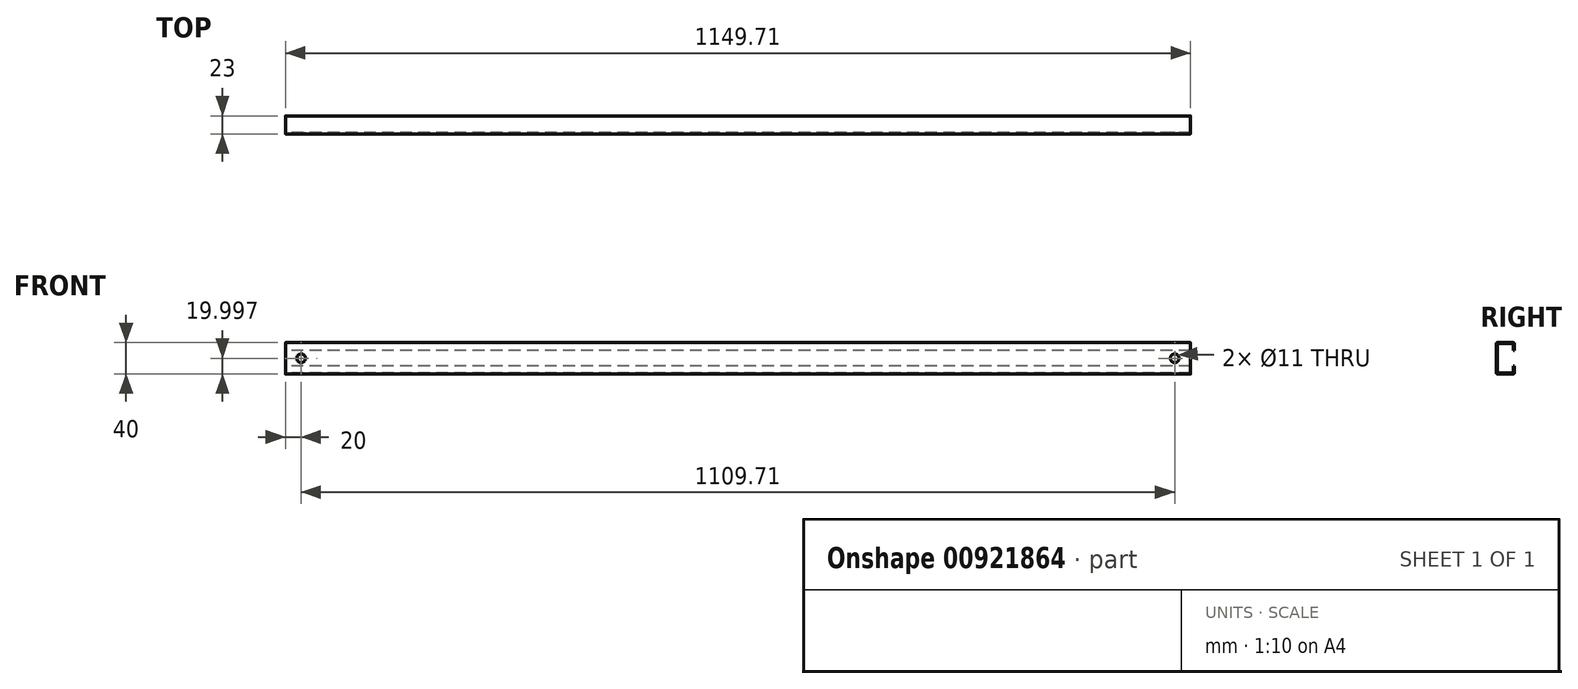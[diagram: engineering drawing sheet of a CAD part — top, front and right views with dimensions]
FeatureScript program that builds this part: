
annotation { "Feature Type Name" : "Feature", "Feature Type Description" : "" }
export const myFeature = defineFeature(function(context is Context, id is Id, definition is map)
    precondition{}
    {
        {
            var Q0;
            Q0=qCreatedBy(makeId("Right.planeOp"),FACE);
            var sketch = newSketch(context, id + "F0", { "sketchPlane" : qUnion([Q0])});
            skPoint(sketch, "E0.visualSharp", {"position": v(-20.15, -12.75) * mm});
            skPoint(sketch, "E1.visualSharp", {"position": v(-18.65, -11.25) * mm});
            skLineSegment(sketch, "E2", {"start": v(9.35, 20.86) * mm, "end": v(-9.65, 20.86) * mm});
            skLineSegment(sketch, "E3", {"start": v(-11.65, 18.86) * mm, "end": v(-11.65, -17.14) * mm});
            skLineSegment(sketch, "E4", {"start": v(-9.65, -19.14) * mm, "end": v(9.35, -19.14) * mm});
            skLineSegment(sketch, "E5", {"start": v(11.35, -17.14) * mm, "end": v(11.35, -9.14) * mm});
            skLineSegment(sketch, "E6", {"start": v(11.35, -9.14) * mm, "end": v(9.85, -9.14) * mm});
            skLineSegment(sketch, "E7", {"start": v(9.85, -9.14) * mm, "end": v(9.85, -16.64) * mm});
            skLineSegment(sketch, "E8", {"start": v(8.85, -17.64) * mm, "end": v(-9.15, -17.64) * mm});
            skLineSegment(sketch, "E9", {"start": v(-9.15, 19.36) * mm, "end": v(8.85, 19.36) * mm});
            skLineSegment(sketch, "E10", {"start": v(9.85, 18.36) * mm, "end": v(9.85, 10.86) * mm});
            skLineSegment(sketch, "E11", {"start": v(9.85, 10.86) * mm, "end": v(11.35, 10.86) * mm});
            skLineSegment(sketch, "E12", {"start": v(11.35, 18.86) * mm, "end": v(11.35, 10.86) * mm});
            skLineSegment(sketch, "E13", {"start": v(-10.15, 18.36) * mm, "end": v(-10.15, -16.64) * mm});
            skPoint(sketch, "E14.visualSharp", {"position": v(11.35, 20.86) * mm});
            skArc(sketch, "E14.filletArc", {"start": v(11.35, 18.86) * mm, "mid": v(10.76, 20.27) * mm, "end": v(9.35, 20.86) * mm});
            skPoint(sketch, "E15.visualSharp", {"position": v(11.35, -19.14) * mm});
            skArc(sketch, "E15.filletArc", {"start": v(9.35, -19.14) * mm, "mid": v(10.76, -18.56) * mm, "end": v(11.35, -17.14) * mm});
            skPoint(sketch, "E16.visualSharp", {"position": v(-11.65, -19.14) * mm});
            skArc(sketch, "E16.filletArc", {"start": v(-11.65, -17.14) * mm, "mid": v(-11.06, -18.56) * mm, "end": v(-9.65, -19.14) * mm});
            skPoint(sketch, "E17.visualSharp", {"position": v(-11.65, 20.86) * mm});
            skArc(sketch, "E17.filletArc", {"start": v(-9.65, 20.86) * mm, "mid": v(-11.06, 20.27) * mm, "end": v(-11.65, 18.86) * mm});
            skPoint(sketch, "E18.visualSharp", {"position": v(-10.15, 19.36) * mm});
            skArc(sketch, "E18.filletArc", {"start": v(-9.15, 19.36) * mm, "mid": v(-9.86, 19.06) * mm, "end": v(-10.15, 18.36) * mm});
            skPoint(sketch, "E19.visualSharp", {"position": v(9.85, 19.36) * mm});
            skArc(sketch, "E19.filletArc", {"start": v(9.85, 18.36) * mm, "mid": v(9.56, 19.06) * mm, "end": v(8.85, 19.36) * mm});
            skPoint(sketch, "E20.visualSharp", {"position": v(9.85, -17.64) * mm});
            skArc(sketch, "E20.filletArc", {"start": v(8.85, -17.64) * mm, "mid": v(9.56, -17.35) * mm, "end": v(9.85, -16.64) * mm});
            skPoint(sketch, "E21.visualSharp", {"position": v(-10.15, -17.64) * mm});
            skArc(sketch, "E21.filletArc", {"start": v(-10.15, -16.64) * mm, "mid": v(-9.86, -17.35) * mm, "end": v(-9.15, -17.64) * mm});
            skSolve(sketch);
        }
        {
            var Q0;
            Q0=makeQuery(id+"F0.imprint","IMPRINT",FACE,{"disambiguationData":[TD([[makeQuery(id+"F0.imprint","IMPRINT",EDGE,{"derivedFrom":sQuery(id+"F0.wireOp",EDGE,"E2")}),1.0]])]});
            extrude(context, id + "F1", {"entities" : qUnion([Q0]), "depth" : 1149.7 * mm, "offsetDistance" : 25 * mm});
        }
        {
            var Q0;
            Q0=makeQuery(id+"F1.opExtrude","SWEPT_FACE",FACE,{"disambiguationData":[OSD([sQuery(id+"F0.wireOp",EDGE,"E3")])]});
            var sketch = newSketch(context, id + "F2", { "sketchPlane" : qUnion([Q0])});
            skCircle(sketch, "E22", {"center": v(1129.7, 0.86) * mm, "radius": 4.31 * mm});
            skCircle(sketch, "E23", {"center": v(20, 0.86) * mm, "radius": 4.31 * mm});
            skSolve(sketch);
        }
        {
            var Q0;
            Q0=sQuery(id+"F2.wireOp",VERTEX,"E23.center");
            var Q1;
            Q1=sQuery(id+"F2.wireOp",VERTEX,"E22.center");
            var Q2;
            Q2=makeQuery(id+"F1.opExtrude","SWEPT_BODY",BODY,{"disambiguationData":[OSD([sQuery(id+"F0.wireOp",EDGE,"E2"),sQuery(id+"F0.wireOp",EDGE,"E3"),sQuery(id+"F0.wireOp",EDGE,"E4"),sQuery(id+"F0.wireOp",EDGE,"E5"),sQuery(id+"F0.wireOp",EDGE,"E6"),sQuery(id+"F0.wireOp",EDGE,"E7"),sQuery(id+"F0.wireOp",EDGE,"E8"),sQuery(id+"F0.wireOp",EDGE,"E9"),sQuery(id+"F0.wireOp",EDGE,"E10"),sQuery(id+"F0.wireOp",EDGE,"E11"),sQuery(id+"F0.wireOp",EDGE,"E12"),sQuery(id+"F0.wireOp",EDGE,"E13"),sQuery(id+"F0.wireOp",EDGE,"E14.filletArc"),sQuery(id+"F0.wireOp",EDGE,"E15.filletArc"),sQuery(id+"F0.wireOp",EDGE,"E16.filletArc"),sQuery(id+"F0.wireOp",EDGE,"E17.filletArc"),sQuery(id+"F0.wireOp",EDGE,"E18.filletArc"),sQuery(id+"F0.wireOp",EDGE,"E19.filletArc"),sQuery(id+"F0.wireOp",EDGE,"E20.filletArc"),sQuery(id+"F0.wireOp",EDGE,"E21.filletArc")])]});
            hole(context, id + "F3", {"style" : HoleStyle.SIMPLE, "endStyle" : HoleEndStyle.THROUGH, "holeDiameter" : 11 * mm, "majorDiameter" : 5 * mm, "isTappedThrough" : true, "tappedDepth" : 12 * mm, "tapClearance" : 3, "locations" : qUnion([Q0, Q1]), "scope" : qUnion([Q2])});
        }
    });
